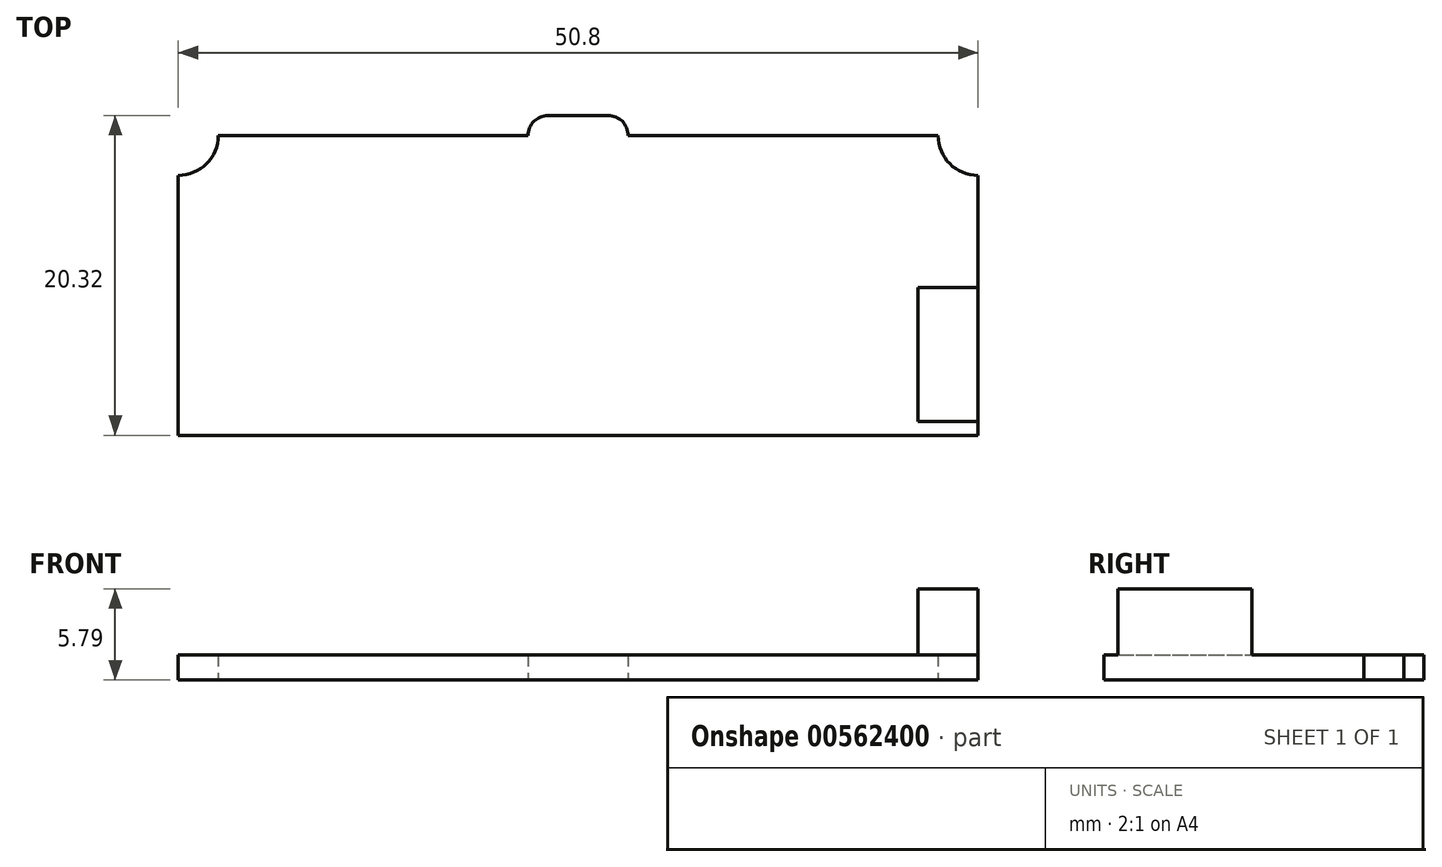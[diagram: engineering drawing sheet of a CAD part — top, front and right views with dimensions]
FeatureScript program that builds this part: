
annotation { "Feature Type Name" : "Feature", "Feature Type Description" : "" }
export const myFeature = defineFeature(function(context is Context, id is Id, definition is map)
    precondition{}
    {
        {
            var Q0;
            Q0=qCreatedBy(makeId("Top.planeOp"),FACE);
            var sketch = newSketch(context, id + "F0", { "sketchPlane" : qUnion([Q0])});
            skLineSegment(sketch, "E0.bottom", {"start": v(-25.4, 0) * mm, "end": v(25.4, 0) * mm});
            skLineSegment(sketch, "E0.top", {"start": v(-22.86, 19.05) * mm, "end": v(-3.18, 19.05) * mm});
            skLineSegment(sketch, "E0.left", {"start": v(-25.4, 0) * mm, "end": v(-25.4, 16.51) * mm});
            skLineSegment(sketch, "E0.right", {"start": v(25.4, 0) * mm, "end": v(25.4, 16.51) * mm});
            skArc(sketch, "E1", {"start": v(-25.4, 16.51) * mm, "mid": v(-23.6, 17.25) * mm, "end": v(-22.86, 19.05) * mm});
            skArc(sketch, "E2", {"start": v(22.86, 19.05) * mm, "mid": v(23.6, 17.25) * mm, "end": v(25.4, 16.51) * mm});
            skLineSegment(sketch, "E3.top", {"start": v(-1.9, 20.32) * mm, "end": v(1.9, 20.32) * mm});
            skLineSegment(sketch, "E3.left", {"start": v(-3.17, 19.05) * mm, "end": v(-3.17, 19.05) * mm});
            skLineSegment(sketch, "E3.right", {"start": v(3.17, 19.05) * mm, "end": v(3.17, 19.05) * mm});
            skLineSegment(sketch, "E4.trimOffspring", {"start": v(3.18, 19.05) * mm, "end": v(22.86, 19.05) * mm});
            skPoint(sketch, "E5", {"position": v(0, 20.32) * mm});
            skPoint(sketch, "E6.visualSharp", {"position": v(-3.17, 20.32) * mm});
            skArc(sketch, "E6.filletArc", {"start": v(-1.9, 20.32) * mm, "mid": v(-2.8, 19.95) * mm, "end": v(-3.18, 19.05) * mm});
            skPoint(sketch, "E7.visualSharp", {"position": v(3.18, 20.32) * mm});
            skArc(sketch, "E7.filletArc", {"start": v(3.17, 19.05) * mm, "mid": v(2.8, 19.95) * mm, "end": v(1.9, 20.32) * mm});
            skSolve(sketch);
        }
        {
            var Q0;
            Q0=makeQuery(id+"F0.imprint","IMPRINT",FACE,{"disambiguationData":[TD([[makeQuery(id+"F0.imprint","IMPRINT",EDGE,{"derivedFrom":sQuery(id+"F0.wireOp",EDGE,"E0.bottom")}),1.0]])]});
            extrude(context, id + "F1", {"entities" : qUnion([Q0]), "depth" : 1.6 * mm, "offsetDistance" : 25.4 * mm});
        }
        {
            var Q0;
            Q0=makeQuery(id+"F1.opExtrude","CAP_FACE",FACE,{"disambiguationData":[OSD([sQuery(id+"F0.wireOp",EDGE,"E0.bottom"),sQuery(id+"F0.wireOp",EDGE,"E0.top"),sQuery(id+"F0.wireOp",EDGE,"E0.left"),sQuery(id+"F0.wireOp",EDGE,"E0.right"),sQuery(id+"F0.wireOp",EDGE,"E1"),sQuery(id+"F0.wireOp",EDGE,"E2"),sQuery(id+"F0.wireOp",EDGE,"E3.top"),sQuery(id+"F0.wireOp",EDGE,"E4.trimOffspring"),sQuery(id+"F0.wireOp",EDGE,"E6.filletArc"),sQuery(id+"F0.wireOp",EDGE,"E7.filletArc")])],"isStart":false});
            var sketch = newSketch(context, id + "F2", { "sketchPlane" : qUnion([Q0])});
            skLineSegment(sketch, "E8.bottom", {"start": v(25.4, 0.89) * mm, "end": v(21.59, 0.89) * mm});
            skLineSegment(sketch, "E8.top", {"start": v(25.4, 9.4) * mm, "end": v(21.59, 9.4) * mm});
            skLineSegment(sketch, "E8.left", {"start": v(25.4, 0.89) * mm, "end": v(25.4, 9.4) * mm});
            skLineSegment(sketch, "E8.right", {"start": v(21.59, 0.89) * mm, "end": v(21.59, 9.4) * mm});
            skSolve(sketch);
        }
        {
            var Q0;
            Q0=makeQuery(id+"F2.imprint","IMPRINT",FACE,{"disambiguationData":[TD([[makeQuery(id+"F2.imprint","IMPRINT",EDGE,{"derivedFrom":sQuery(id+"F2.wireOp",EDGE,"E8.bottom")}),-1.0]])]});
            extrude(context, id + "F3", {"entities" : qUnion([Q0]), "operationType" : NewBodyOperationType.ADD, "depth" : 4.2 * mm, "offsetDistance" : 25.4 * mm});
        }
    });
